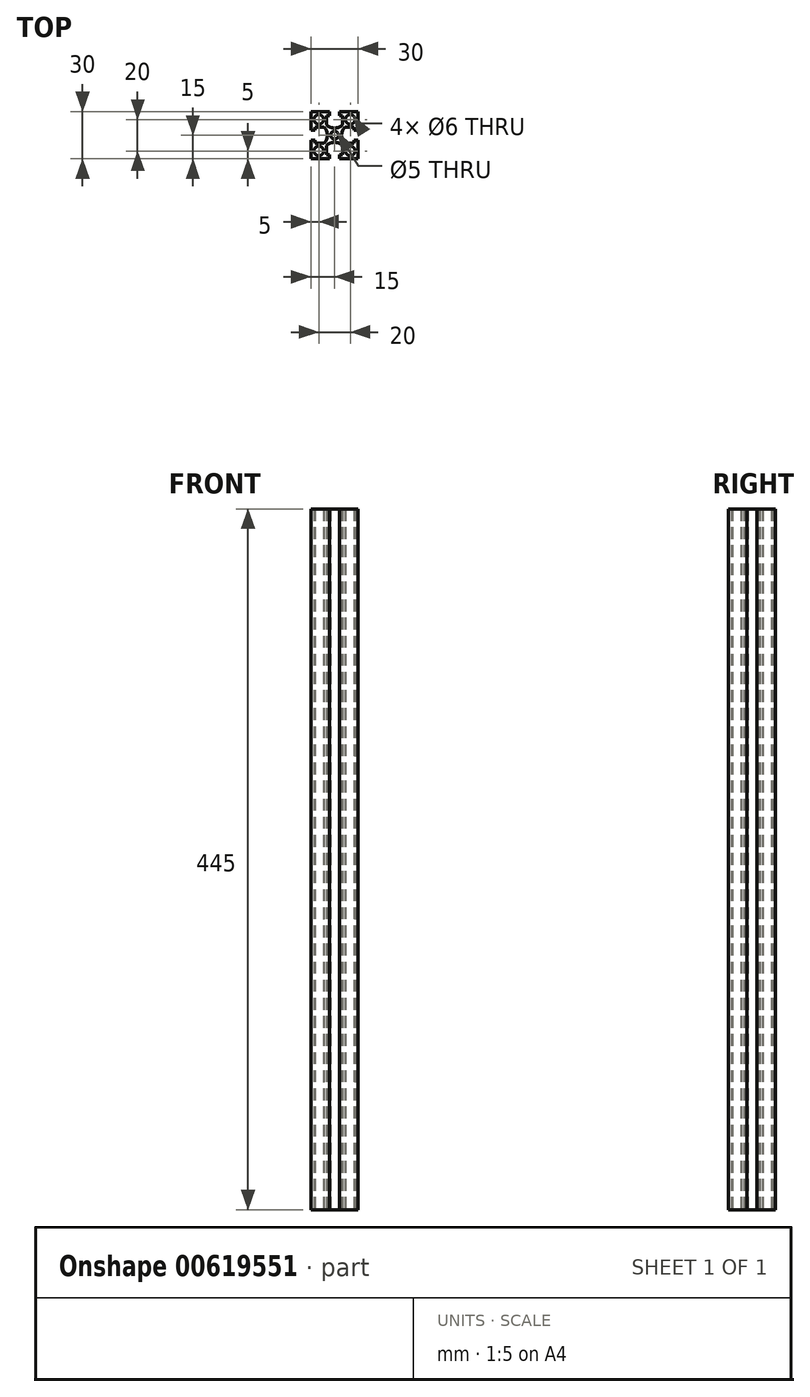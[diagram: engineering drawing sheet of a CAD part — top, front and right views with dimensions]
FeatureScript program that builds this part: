
annotation { "Feature Type Name" : "Feature", "Feature Type Description" : "" }
export const myFeature = defineFeature(function(context is Context, id is Id, definition is map)
    precondition{}
    {
        {
            var Q0;
            Q0=qCreatedBy(makeId("Top.planeOp"),FACE);
            var sketch = newSketch(context, id + "F0", { "sketchPlane" : qUnion([Q0])});
            skCircle(sketch, "E0", {"center": v(-10, 10) * mm, "radius": 3 * mm});
            skCircle(sketch, "E1.MirrorC", {"center": v(-10, -10) * mm, "radius": 3 * mm});
            skLineSegment(sketch, "E2.top", {"start": v(-15, 3.15) * mm, "end": v(-15, -3.15) * mm});
            skLineSegment(sketch, "E2.left", {"start": v(-12.5, 3.15) * mm, "end": v(-15, 3.15) * mm});
            skLineSegment(sketch, "E2.right", {"start": v(-12.5, -3.15) * mm, "end": v(-15, -3.15) * mm});
            skLineSegment(sketch, "E3.bottom", {"start": v(-12.5, 5.15) * mm, "end": v(-12.5, 3.15) * mm});
            skLineSegment(sketch, "E3.left", {"start": v(-12.5, 5.15) * mm, "end": v(-6.55, 5.15) * mm});
            skLineSegment(sketch, "E3.right", {"start": v(-12.5, -5.15) * mm, "end": v(-6.55, -5.15) * mm});
            skArc(sketch, "E4", {"start": v(-6.55, -5.15) * mm, "mid": v(-4.5, 0) * mm, "end": v(-6.55, 5.15) * mm});
            skLineSegment(sketch, "E5.trimOffspring", {"start": v(-12.5, -3.15) * mm, "end": v(-12.5, -5.15) * mm});
            skLineSegment(sketch, "E6.bottom", {"start": v(15, -15) * mm, "end": v(-15, -15) * mm});
            skLineSegment(sketch, "E6.top", {"start": v(15, 15) * mm, "end": v(-15, 15) * mm});
            skLineSegment(sketch, "E6.left", {"start": v(15, -15) * mm, "end": v(15, 15) * mm});
            skLineSegment(sketch, "E6.right", {"start": v(-15, -15) * mm, "end": v(-15, 15) * mm});
            skPoint(sketch, "E6.middle", {"position": v(0, 0) * mm});
            skCircle(sketch, "E7.MirrorC", {"center": v(10, 10) * mm, "radius": 3 * mm});
            skCircle(sketch, "E8.MirrorC", {"center": v(10, -10) * mm, "radius": 3 * mm});
            skLineSegment(sketch, "E9.1.0", {"start": v(-5.15, -12.5) * mm, "end": v(-3.15, -12.5) * mm});
            skArc(sketch, "E9.1.1", {"start": v(5.15, -6.55) * mm, "mid": v(0, -4.5) * mm, "end": v(-5.15, -6.55) * mm});
            skLineSegment(sketch, "E9.1.2", {"start": v(-3.15, -15) * mm, "end": v(3.15, -15) * mm});
            skLineSegment(sketch, "E9.1.3", {"start": v(-3.15, -12.5) * mm, "end": v(-3.15, -15) * mm});
            skLineSegment(sketch, "E9.1.4", {"start": v(-5.15, -12.5) * mm, "end": v(-5.15, -6.55) * mm});
            skLineSegment(sketch, "E9.1.5", {"start": v(3.15, -12.5) * mm, "end": v(5.15, -12.5) * mm});
            skLineSegment(sketch, "E9.1.6", {"start": v(5.15, -12.5) * mm, "end": v(5.15, -6.55) * mm});
            skLineSegment(sketch, "E9.1.7", {"start": v(3.15, -12.5) * mm, "end": v(3.15, -15) * mm});
            skLineSegment(sketch, "E9.2.0", {"start": v(12.5, -5.15) * mm, "end": v(12.5, -3.15) * mm});
            skArc(sketch, "E9.2.1", {"start": v(6.55, 5.15) * mm, "mid": v(4.5, 0) * mm, "end": v(6.55, -5.15) * mm});
            skLineSegment(sketch, "E9.2.2", {"start": v(15, -3.15) * mm, "end": v(15, 3.15) * mm});
            skLineSegment(sketch, "E9.2.3", {"start": v(12.5, -3.15) * mm, "end": v(15, -3.15) * mm});
            skLineSegment(sketch, "E9.2.4", {"start": v(12.5, -5.15) * mm, "end": v(6.55, -5.15) * mm});
            skLineSegment(sketch, "E9.2.5", {"start": v(12.5, 3.15) * mm, "end": v(12.5, 5.15) * mm});
            skLineSegment(sketch, "E9.2.6", {"start": v(12.5, 5.15) * mm, "end": v(6.55, 5.15) * mm});
            skLineSegment(sketch, "E9.2.7", {"start": v(12.5, 3.15) * mm, "end": v(15, 3.15) * mm});
            skLineSegment(sketch, "E9.3.0", {"start": v(5.15, 12.5) * mm, "end": v(3.15, 12.5) * mm});
            skArc(sketch, "E9.3.1", {"start": v(-5.15, 6.55) * mm, "mid": v(0, 4.5) * mm, "end": v(5.15, 6.55) * mm});
            skLineSegment(sketch, "E9.3.2", {"start": v(3.15, 15) * mm, "end": v(-3.15, 15) * mm});
            skLineSegment(sketch, "E9.3.3", {"start": v(3.15, 12.5) * mm, "end": v(3.15, 15) * mm});
            skLineSegment(sketch, "E9.3.4", {"start": v(5.15, 12.5) * mm, "end": v(5.15, 6.55) * mm});
            skLineSegment(sketch, "E9.3.5", {"start": v(-3.15, 12.5) * mm, "end": v(-5.15, 12.5) * mm});
            skLineSegment(sketch, "E9.3.6", {"start": v(-5.15, 12.5) * mm, "end": v(-5.15, 6.55) * mm});
            skLineSegment(sketch, "E9.3.7", {"start": v(-3.15, 12.5) * mm, "end": v(-3.15, 15) * mm});
            skCircle(sketch, "E10", {"center": v(0, 0) * mm, "radius": 2.5 * mm});
            skSolve(sketch);
        }
        {
            var Q0;
            Q0=makeQuery(id+"F0.imprint","IMPRINT",FACE,{"disambiguationData":[TD([[makeQuery(id+"F0.imprint","IMPRINT",EDGE,{"derivedFrom":sQuery(id+"F0.wireOp",EDGE,"E0")}),-1.0]])]});
            extrude(context, id + "F1", {"entities" : qUnion([Q0]), "depth" : 445 * mm, "offsetDistance" : 25 * mm});
        }
    });
